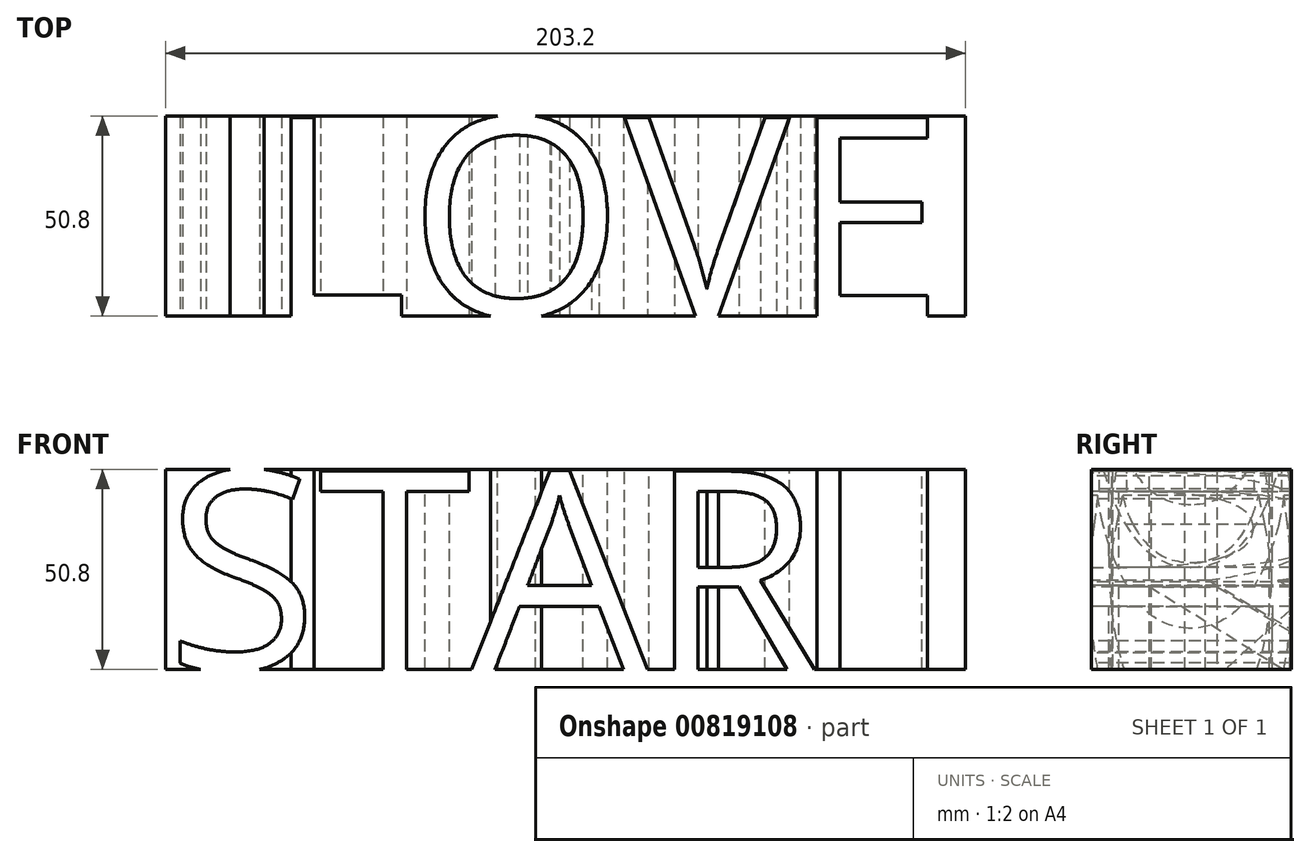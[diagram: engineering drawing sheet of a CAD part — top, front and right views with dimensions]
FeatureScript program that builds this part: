
annotation { "Feature Type Name" : "Feature", "Feature Type Description" : "" }
export const myFeature = defineFeature(function(context is Context, id is Id, definition is map)
    precondition{}
    {
        {
            var Q0;
            Q0=qCreatedBy(makeId("Front.planeOp"),FACE);
            var sketch = newSketch(context, id + "F0", { "sketchPlane" : qUnion([Q0])});
            skLineSegment(sketch, "E0.bottom", {"start": v(-101.6, 25.4) * mm, "end": v(101.6, 25.4) * mm});
            skLineSegment(sketch, "E0.top", {"start": v(-101.6, -25.4) * mm, "end": v(101.6, -25.4) * mm});
            skLineSegment(sketch, "E0.left", {"start": v(-101.6, 25.4) * mm, "end": v(-101.6, -25.4) * mm});
            skLineSegment(sketch, "E0.right", {"start": v(101.6, 25.4) * mm, "end": v(101.6, -25.4) * mm});
            skPoint(sketch, "E0.middle", {"position": v(0, 0) * mm});
            skSolve(sketch);
        }
        {
            var Q0;
            Q0 = qSketchRegion(id + "F0", true);
            extrude(context, id + "F1", {"entities" : qUnion([Q0]), "endBound" : BoundingType.SYMMETRIC, "depth" : 50.8 * mm, "offsetDistance" : 25.4 * mm});
        }
        {
            var Q0;
            Q0=makeQuery(id+"F1.opExtrude","CAP_FACE",FACE,{"disambiguationData":[OSD([sQuery(id+"F0.wireOp",EDGE,"E0.bottom"),sQuery(id+"F0.wireOp",EDGE,"E0.top"),sQuery(id+"F0.wireOp",EDGE,"E0.left"),sQuery(id+"F0.wireOp",EDGE,"E0.right")])],"isStart":false});
            var sketch = newSketch(context, id + "F2", { "sketchPlane" : qUnion([Q0])});
            skText(sketch, "E1", { "text": "STAR\n", "fontName": "OpenSans-Regular.ttf"});
            const initialGuessF2  = {"E1": [-0.1016, -0.0254, 1, 0, 0.0508]};
            skSetInitialGuess(sketch, initialGuessF2);
            skSolve(sketch);
        }
        {
            var Q0;
            Q0 = qSketchRegion(id + "F2", true);
            extrude(context, id + "F3", {"entities" : qUnion([Q0]), "operationType" : NewBodyOperationType.REMOVE, "endBound" : BoundingType.THROUGH_ALL, "oppositeDirection" : true, "depth" : 25.4 * mm, "offsetDistance" : 25.4 * mm});
        }
        {
            var Q0;
            {var subQ0=sQuery(id+"F0.wireOp",EDGE,"E0.right");var subQ3=sQuery(id+"F0.wireOp",EDGE,"E0.bottom");Q0=makeQuery(id+"F3.boolean.opBoolean","SPLIT",FACE,{"disambiguationData":[TD([makeQuery(id+"F1.opExtrude","SWEPT_FACE",FACE,{"disambiguationData":[OSD([subQ0])]})])],"derivedFrom":makeQuery(id+"F1.opExtrude","SWEPT_FACE",FACE,{"disambiguationData":[OSD([subQ3])]})});}
            var sketch = newSketch(context, id + "F4", { "sketchPlane" : qUnion([Q0])});
            skText(sketch, "E2", { "text": "LOVE", "fontName": "OpenSans-Regular.ttf"});
            const initialGuessF4  = {"E2": [-0.07662, -0.0254, 1, 0, 0.0508]};
            skSetInitialGuess(sketch, initialGuessF4);
            skSolve(sketch);
        }
        {
            var Q0;
            Q0 = qSketchRegion(id + "F4", true);
            extrude(context, id + "F5", {"entities" : qUnion([Q0]), "operationType" : NewBodyOperationType.REMOVE, "endBound" : BoundingType.THROUGH_ALL, "oppositeDirection" : true, "depth" : 25.4 * mm, "offsetDistance" : 25.4 * mm});
        }
    });
